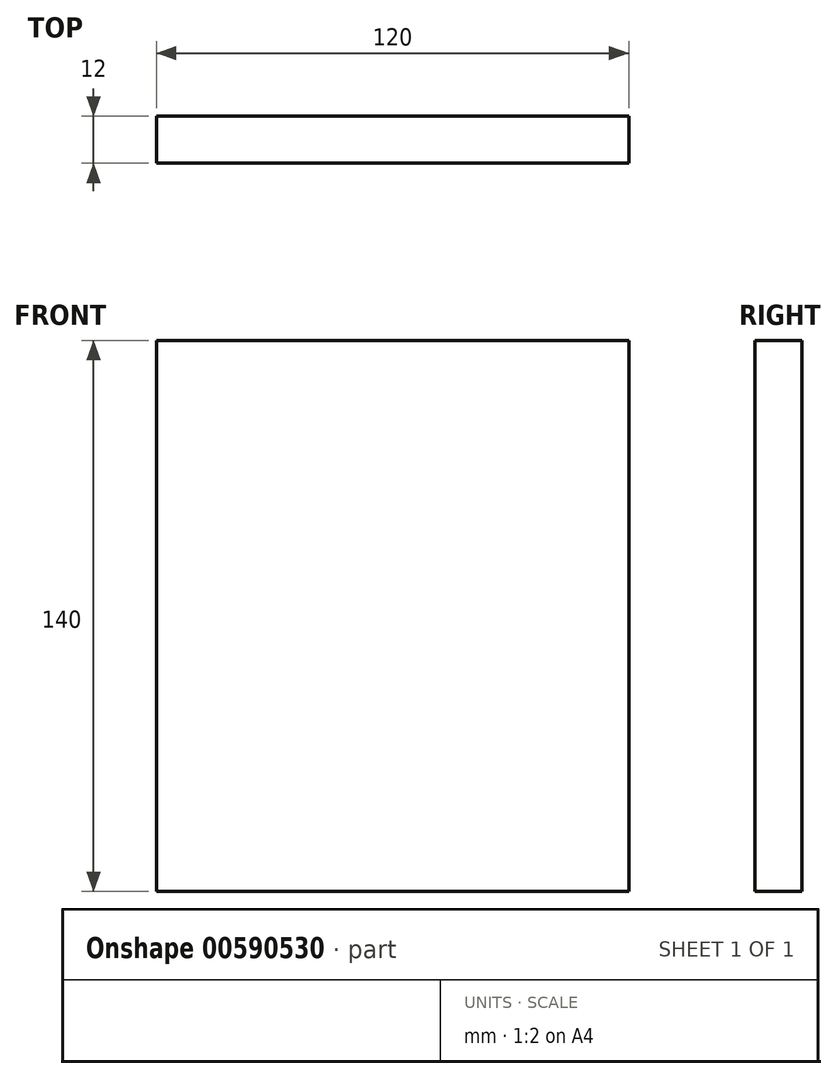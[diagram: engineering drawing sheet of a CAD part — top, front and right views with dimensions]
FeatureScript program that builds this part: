
annotation { "Feature Type Name" : "Feature", "Feature Type Description" : "" }
export const myFeature = defineFeature(function(context is Context, id is Id, definition is map)
    precondition{}
    {
        {
            var Q0;
            Q0=qCreatedBy(makeId("Front.planeOp"),FACE);
            var sketch = newSketch(context, id + "F0", { "sketchPlane" : qUnion([Q0])});
            skLineSegment(sketch, "E0.bottom", {"start": v(-64.3, 60.36) * mm, "end": v(55.7, 60.36) * mm});
            skLineSegment(sketch, "E0.top", {"start": v(-64.3, -79.64) * mm, "end": v(55.7, -79.64) * mm});
            skLineSegment(sketch, "E0.left", {"start": v(-64.3, 60.36) * mm, "end": v(-64.3, -79.64) * mm});
            skLineSegment(sketch, "E0.right", {"start": v(55.7, 60.36) * mm, "end": v(55.7, -79.64) * mm});
            skSolve(sketch);
        }
        {
            var Q0;
            Q0 = qSketchRegion(id + "F0", true);
            extrude(context, id + "F1", {"entities" : qUnion([Q0]), "depth" : 12 * mm, "offsetDistance" : 25 * mm});
        }
    });
